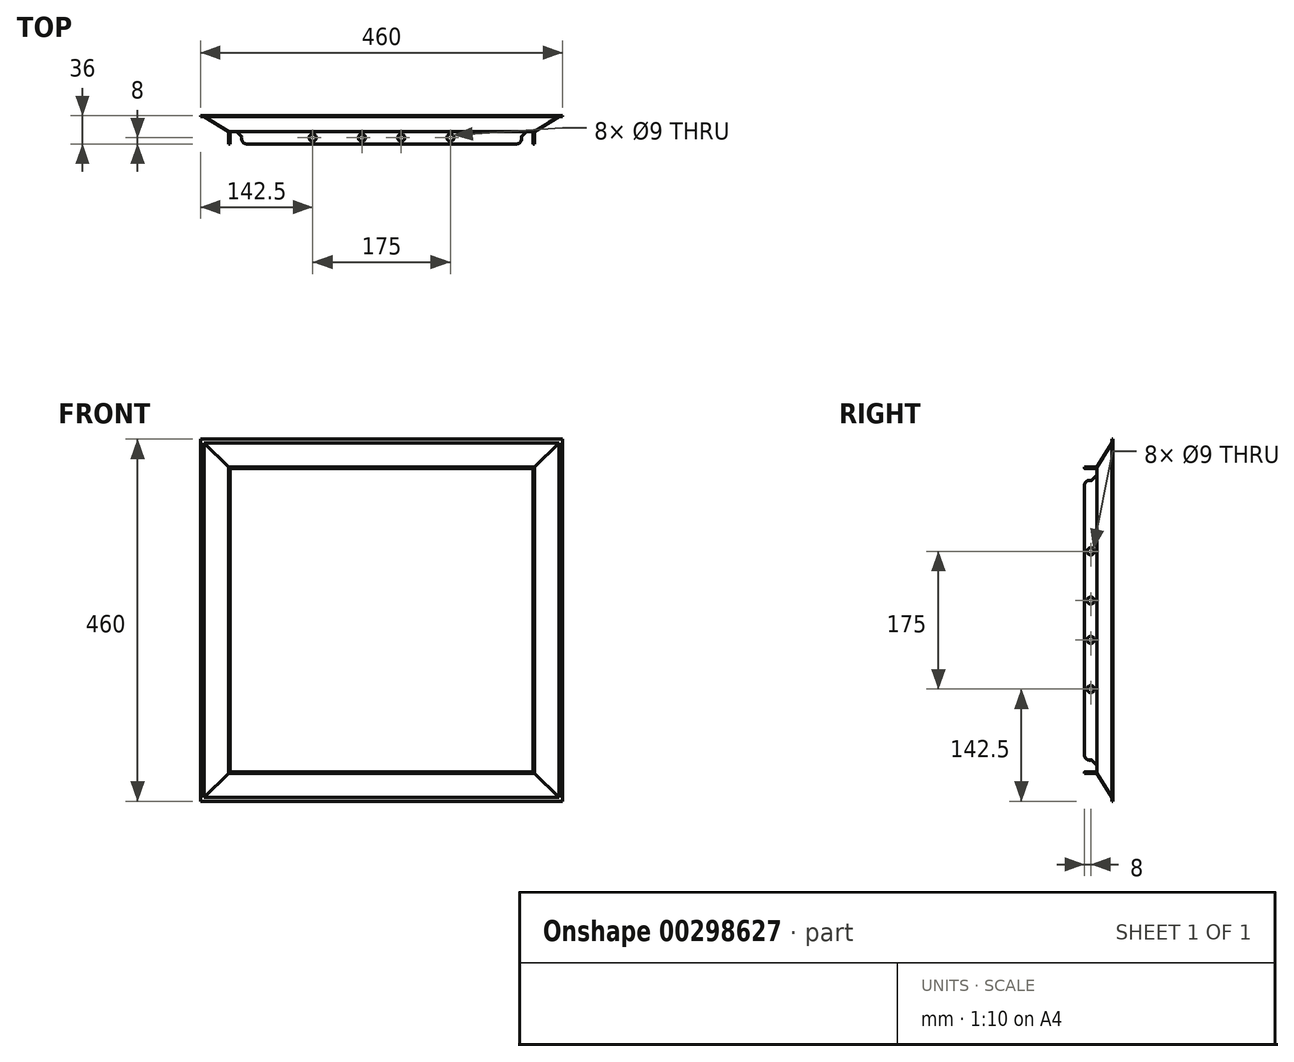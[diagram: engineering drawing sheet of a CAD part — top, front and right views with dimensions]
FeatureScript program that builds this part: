
annotation { "Feature Type Name" : "Feature", "Feature Type Description" : "" }
export const myFeature = defineFeature(function(context is Context, id is Id, definition is map)
    precondition{}
    {
        {
            var Q0;
            Q0=qCreatedBy(makeId("Front.planeOp"),FACE);
            var sketch = newSketch(context, id + "F0", { "sketchPlane" : qUnion([Q0])});
            skLineSegment(sketch, "E0.bottom", {"start": v(-230, 230) * mm, "end": v(230, 230) * mm});
            skLineSegment(sketch, "E0.top", {"start": v(-230, -230) * mm, "end": v(230, -230) * mm});
            skLineSegment(sketch, "E0.left", {"start": v(-230, 230) * mm, "end": v(-230, -230) * mm});
            skLineSegment(sketch, "E0.right", {"start": v(230, 230) * mm, "end": v(230, -230) * mm});
            skLineSegment(sketch, "E1.bottom", {"start": v(225, -225) * mm, "end": v(-225, -225) * mm});
            skLineSegment(sketch, "E1.top", {"start": v(225, 225) * mm, "end": v(-225, 225) * mm});
            skLineSegment(sketch, "E1.left", {"start": v(225, -225) * mm, "end": v(225, 225) * mm});
            skLineSegment(sketch, "E1.right", {"start": v(-225, -225) * mm, "end": v(-225, 225) * mm});
            skPoint(sketch, "E1.middle", {"position": v(0, 0) * mm});
            skLineSegment(sketch, "E2", {"start": v(442.73, 0) * mm, "end": v(-380.23, 0) * mm, "construction": true});
            skPoint(sketch, "E2.endSnap0", {"position": v(-225, 0) * mm});
            skLineSegment(sketch, "E3", {"start": v(0, -299.1) * mm, "end": v(0, 337.98) * mm, "construction": true});
            skSolve(sketch);
        }
        {
            var Q0;
            Q0=makeQuery(id+"F0.imprint","IMPRINT",FACE,{"disambiguationData":[TD([[makeQuery(id+"F0.imprint","IMPRINT",EDGE,{"derivedFrom":sQuery(id+"F0.wireOp",EDGE,"E0.bottom")}),-1.0]])]});
            cPlane(context, id + "F1", {"entities" : qUnion([Q0]), "cplaneType" : CPlaneType.OFFSET, "offset" : 20 * mm, "width" : 150 * mm, "height" : 150 * mm});
        }
        {
            var Q0;
            Q0=qCreatedBy(id+"F1.planeOp",FACE);
            var sketch = newSketch(context, id + "F2", { "sketchPlane" : qUnion([Q0])});
            skLineSegment(sketch, "E4.bottom", {"start": v(192.5, -192.5) * mm, "end": v(-192.5, -192.5) * mm});
            skLineSegment(sketch, "E4.top", {"start": v(192.5, 192.5) * mm, "end": v(-192.5, 192.5) * mm});
            skLineSegment(sketch, "E4.left", {"start": v(192.5, -192.5) * mm, "end": v(192.5, 192.5) * mm});
            skLineSegment(sketch, "E4.right", {"start": v(-192.5, -192.5) * mm, "end": v(-192.5, 192.5) * mm});
            skPoint(sketch, "E4.middle", {"position": v(0, 0) * mm});
            skSolve(sketch);
        }
        {
            var Q0;
            Q0=makeQuery(id+"F0.imprint","IMPRINT",FACE,{"disambiguationData":[TD([[makeQuery(id+"F0.imprint","IMPRINT",EDGE,{"derivedFrom":sQuery(id+"F0.wireOp",EDGE,"E1.bottom")}),-1.0]])]});
            var Q1;
            Q1=makeQuery(id+"F2.imprint","IMPRINT",FACE,{"disambiguationData":[TD([[makeQuery(id+"F2.imprint","IMPRINT",EDGE,{"derivedFrom":sQuery(id+"F2.wireOp",EDGE,"E4.bottom")}),-1.0]])]});
            loft(context, id + "F3", {"sheetProfilesArray" : [{ "sheetProfileEntities" : qUnion([Q0]) }, { "sheetProfileEntities" : qUnion([Q1]) }]});
        }
        {
            var Q0;
            Q0=makeQuery(id+"F3.opLoft","CAP_FACE",FACE,{"disambiguationData":[OSD([makeQuery(id+"F2.imprint","IMPRINT",FACE,{"disambiguationData":[TD([[makeQuery(id+"F2.imprint","IMPRINT",EDGE,{"derivedFrom":sQuery(id+"F2.wireOp",EDGE,"E4.bottom")}),-1.0]])]})])],"isStart":true});
            var Q1;
            Q1=makeQuery(id+"F3.opLoft","CAP_FACE",FACE,{"disambiguationData":[OSD([makeQuery(id+"F0.imprint","IMPRINT",FACE,{"disambiguationData":[TD([[makeQuery(id+"F0.imprint","IMPRINT",EDGE,{"derivedFrom":sQuery(id+"F0.wireOp",EDGE,"E1.bottom")}),-1.0]])]})])],"isStart":true});
            shell(context, id + "F4", {"entities" : qUnion([Q0, Q1]), "thickness" : 1 * mm, "oppositeDirection" : true});
        }
        {
            var Q0;
            Q0=makeQuery(id+"F0.imprint","IMPRINT",FACE,{"disambiguationData":[TD([[makeQuery(id+"F0.imprint","IMPRINT",EDGE,{"derivedFrom":sQuery(id+"F0.wireOp",EDGE,"E0.bottom")}),-1.0]])]});
            extrude(context, id + "F5", {"entities" : qUnion([Q0]), "operationType" : NewBodyOperationType.ADD, "depth" : 1 * mm});
        }
        {
            var Q0;
            Q0=makeQuery(id+"F3.opLoft","CAP_FACE",FACE,{"disambiguationData":[OSD([makeQuery(id+"F2.imprint","IMPRINT",FACE,{"disambiguationData":[TD([[makeQuery(id+"F2.imprint","IMPRINT",EDGE,{"derivedFrom":sQuery(id+"F2.wireOp",EDGE,"E4.bottom")}),-1.0]])]})])],"isStart":true});
            var sketch = newSketch(context, id + "F6", { "sketchPlane" : qUnion([Q0])});
            skLineSegment(sketch, "E5.0", {"start": v(-192.5, -192.5) * mm, "end": v(192.5, -192.5) * mm});
            skLineSegment(sketch, "E6.0", {"start": v(192.5, -192.5) * mm, "end": v(192.5, 192.5) * mm});
            skLineSegment(sketch, "E7.0", {"start": v(194.4, -194.4) * mm, "end": v(194.4, 194.4) * mm});
            skLineSegment(sketch, "E8.0", {"start": v(194.4, 194.4) * mm, "end": v(-194.4, 194.4) * mm});
            skLineSegment(sketch, "E9.0", {"start": v(192.5, 192.5) * mm, "end": v(-192.5, 192.5) * mm});
            skLineSegment(sketch, "E10.0", {"start": v(-194.4, 194.4) * mm, "end": v(-194.4, -194.4) * mm});
            skLineSegment(sketch, "E11.0", {"start": v(-192.5, 192.5) * mm, "end": v(-192.5, -192.5) * mm});
            skLineSegment(sketch, "E12.0", {"start": v(-194.4, -194.4) * mm, "end": v(194.4, -194.4) * mm});
            skSolve(sketch);
        }
        {
            var Q0;
            Q0 = qSketchRegion(id + "F6", true);
            extrude(context, id + "F7", {"entities" : qUnion([Q0]), "operationType" : NewBodyOperationType.ADD, "depth" : 16 * mm});
        }
        {
            var Q0;
            Q0=makeQuery(id+"F7.opExtrude","SWEPT_FACE",FACE,{"disambiguationData":[OSD([sQuery(id+"F6.wireOp",EDGE,"E8.0")])]});
            var sketch = newSketch(context, id + "F8", { "sketchPlane" : qUnion([Q0])});
            skLineSegment(sketch, "E13", {"start": v(194.4, -20) * mm, "end": v(184.4, -20) * mm});
            skLineSegment(sketch, "E14", {"start": v(184.4, -20) * mm, "end": v(177.34, -27.07) * mm});
            skArc(sketch, "E15", {"start": v(171.02, -36) * mm, "mid": v(176.49, -33.17) * mm, "end": v(177.34, -27.07) * mm});
            skLineSegment(sketch, "E16", {"start": v(194.4, -20) * mm, "end": v(194.4, -36) * mm});
            skLineSegment(sketch, "E17", {"start": v(171.02, -36) * mm, "end": v(194.4, -36) * mm});
            skLineSegment(sketch, "E18", {"start": v(-194.4, -20) * mm, "end": v(-184.4, -20) * mm});
            skLineSegment(sketch, "E19", {"start": v(-184.4, -20) * mm, "end": v(-177.34, -27.07) * mm});
            skArc(sketch, "E20", {"start": v(-177.34, -27.07) * mm, "mid": v(-176.49, -33.17) * mm, "end": v(-171.02, -36) * mm});
            skLineSegment(sketch, "E21", {"start": v(-171.02, -36) * mm, "end": v(-194.4, -36) * mm});
            skLineSegment(sketch, "E22", {"start": v(-194.4, -36) * mm, "end": v(-194.4, -20) * mm});
            skSolve(sketch);
        }
        {
            var Q0;
            Q0=makeQuery(id+"F8.imprint","IMPRINT",FACE,{"disambiguationData":[TD([[makeQuery(id+"F8.imprint","IMPRINT",EDGE,{"derivedFrom":sQuery(id+"F8.wireOp",EDGE,"E13")}),1.0]])]});
            var Q1;
            Q1=sQuery(id+"F8.wireOp",EDGE,"E16");
            revolve(context, id + "F9", {"operationType" : NewBodyOperationType.REMOVE, "entities" : qUnion([Q0]), "axis" : qUnion([Q1]), "revolveType" : RevolveType.FULL, "oppositeDirection" : true});
        }
        {
            var Q0;
            Q0=makeQuery(id+"F8.imprint","IMPRINT",FACE,{"disambiguationData":[TD([[makeQuery(id+"F8.imprint","IMPRINT",EDGE,{"derivedFrom":sQuery(id+"F8.wireOp",EDGE,"E18")}),1.0]])]});
            var Q1;
            Q1=sQuery(id+"F8.wireOp",EDGE,"E22");
            revolve(context, id + "F10", {"operationType" : NewBodyOperationType.REMOVE, "entities" : qUnion([Q0]), "axis" : qUnion([Q1]), "revolveType" : RevolveType.FULL, "oppositeDirection" : true});
        }
        {
            var Q0;
            Q0=makeQuery(id+"F7.opExtrude","SWEPT_FACE",FACE,{"disambiguationData":[OSD([sQuery(id+"F6.wireOp",EDGE,"E12.0")])]});
            var sketch = newSketch(context, id + "F11", { "sketchPlane" : qUnion([Q0])});
            skLineSegment(sketch, "E23.0", {"start": v(-171.02, 36) * mm, "end": v(-194.4, 36) * mm});
            skArc(sketch, "E24.0", {"start": v(-177.34, 27.07) * mm, "mid": v(-176.49, 33.17) * mm, "end": v(-171.02, 36) * mm});
            skLineSegment(sketch, "E24.1", {"start": v(-194.4, 36) * mm, "end": v(-194.4, 20) * mm});
            skLineSegment(sketch, "E24.2", {"start": v(-184.4, 20) * mm, "end": v(-177.34, 27.07) * mm});
            skLineSegment(sketch, "E25.0", {"start": v(-194.4, 20) * mm, "end": v(-184.4, 20) * mm});
            skLineSegment(sketch, "E26.0", {"start": v(171.02, 36) * mm, "end": v(194.4, 36) * mm});
            skLineSegment(sketch, "E27.0", {"start": v(194.4, 20) * mm, "end": v(194.4, 36) * mm});
            skArc(sketch, "E28.0", {"start": v(171.02, 36) * mm, "mid": v(176.49, 33.17) * mm, "end": v(177.34, 27.07) * mm});
            skLineSegment(sketch, "E29.0", {"start": v(184.4, 20) * mm, "end": v(177.34, 27.07) * mm});
            skLineSegment(sketch, "E30.0", {"start": v(194.4, 20) * mm, "end": v(184.4, 20) * mm});
            skSolve(sketch);
        }
        {
            var Q0;
            Q0=makeQuery(id+"F11.imprint","IMPRINT",FACE,{"disambiguationData":[TD([[makeQuery(id+"F11.imprint","IMPRINT",EDGE,{"derivedFrom":sQuery(id+"F11.wireOp",EDGE,"E26.0")}),-1.0]])]});
            var Q1;
            Q1=sQuery(id+"F11.wireOp",EDGE,"E27.0");
            revolve(context, id + "F12", {"operationType" : NewBodyOperationType.REMOVE, "entities" : qUnion([Q0]), "axis" : qUnion([Q1]), "revolveType" : RevolveType.FULL, "oppositeDirection" : true});
        }
        {
            var Q0;
            Q0=makeQuery(id+"F11.imprint","IMPRINT",FACE,{"disambiguationData":[TD([[makeQuery(id+"F11.imprint","IMPRINT",EDGE,{"derivedFrom":sQuery(id+"F11.wireOp",EDGE,"E23.0")}),-1.0]])]});
            var Q1;
            Q1=sQuery(id+"F11.wireOp",EDGE,"E24.1");
            revolve(context, id + "F13", {"operationType" : NewBodyOperationType.REMOVE, "entities" : qUnion([Q0]), "axis" : qUnion([Q1]), "revolveType" : RevolveType.FULL, "oppositeDirection" : true});
        }
        {
            var Q0;
            Q0=makeQuery(id+"F7.opExtrude","SWEPT_FACE",FACE,{"disambiguationData":[OSD([sQuery(id+"F6.wireOp",EDGE,"E12.0")])]});
            var sketch = newSketch(context, id + "F14", { "sketchPlane" : qUnion([Q0])});
            skLineSegment(sketch, "E31", {"start": v(-272.07, 28) * mm, "end": v(274.69, 28) * mm, "construction": true});
            skCircle(sketch, "E32", {"center": v(-87.5, 28) * mm, "radius": 4.5 * mm});
            skCircle(sketch, "E33", {"center": v(-25, 28) * mm, "radius": 4.5 * mm});
            skCircle(sketch, "E34", {"center": v(25, 28) * mm, "radius": 4.5 * mm});
            skCircle(sketch, "E35", {"center": v(87.5, 28) * mm, "radius": 4.5 * mm});
            skSolve(sketch);
        }
        {
            var Q0;
            Q0=makeQuery(id+"F14.imprint","IMPRINT",FACE,{"disambiguationData":[TD([[makeQuery(id+"F14.imprint","IMPRINT",EDGE,{"derivedFrom":sQuery(id+"F14.wireOp",EDGE,"E32")}),1.0]])]});
            var Q1;
            Q1=makeQuery(id+"F14.imprint","IMPRINT",FACE,{"disambiguationData":[TD([[makeQuery(id+"F14.imprint","IMPRINT",EDGE,{"derivedFrom":sQuery(id+"F14.wireOp",EDGE,"E33")}),1.0]])]});
            var Q2;
            Q2=makeQuery(id+"F14.imprint","IMPRINT",FACE,{"disambiguationData":[TD([[makeQuery(id+"F14.imprint","IMPRINT",EDGE,{"derivedFrom":sQuery(id+"F14.wireOp",EDGE,"E34")}),1.0]])]});
            var Q3;
            Q3=makeQuery(id+"F14.imprint","IMPRINT",FACE,{"disambiguationData":[TD([[makeQuery(id+"F14.imprint","IMPRINT",EDGE,{"derivedFrom":sQuery(id+"F14.wireOp",EDGE,"E35")}),1.0]])]});
            extrude(context, id + "F15", {"entities" : qUnion([Q0, Q1, Q2, Q3]), "operationType" : NewBodyOperationType.REMOVE, "endBound" : BoundingType.THROUGH_ALL, "oppositeDirection" : true, "depth" : 25 * mm});
        }
        {
            var Q0;
            Q0=makeQuery(id+"F7.opExtrude","SWEPT_FACE",FACE,{"disambiguationData":[OSD([sQuery(id+"F6.wireOp",EDGE,"E7.0")])]});
            var sketch = newSketch(context, id + "F16", { "sketchPlane" : qUnion([Q0])});
            skLineSegment(sketch, "E36", {"start": v(-28, -153.4) * mm, "end": v(-28, 164.11) * mm, "construction": true});
            skCircle(sketch, "E37", {"center": v(-28, -87.5) * mm, "radius": 4.5 * mm});
            skCircle(sketch, "E38", {"center": v(-28, -25) * mm, "radius": 4.5 * mm});
            skCircle(sketch, "E39", {"center": v(-28, 25) * mm, "radius": 4.5 * mm});
            skCircle(sketch, "E40", {"center": v(-28, 87.5) * mm, "radius": 4.5 * mm});
            skSolve(sketch);
        }
        {
            var Q0;
            Q0=makeQuery(id+"F16.imprint","IMPRINT",FACE,{"disambiguationData":[TD([[makeQuery(id+"F16.imprint","IMPRINT",EDGE,{"derivedFrom":sQuery(id+"F16.wireOp",EDGE,"E37")}),1.0]])]});
            var Q1;
            Q1=makeQuery(id+"F16.imprint","IMPRINT",FACE,{"disambiguationData":[TD([[makeQuery(id+"F16.imprint","IMPRINT",EDGE,{"derivedFrom":sQuery(id+"F16.wireOp",EDGE,"E38")}),1.0]])]});
            var Q2;
            Q2=makeQuery(id+"F16.imprint","IMPRINT",FACE,{"disambiguationData":[TD([[makeQuery(id+"F16.imprint","IMPRINT",EDGE,{"derivedFrom":sQuery(id+"F16.wireOp",EDGE,"E39")}),1.0]])]});
            var Q3;
            Q3=makeQuery(id+"F16.imprint","IMPRINT",FACE,{"disambiguationData":[TD([[makeQuery(id+"F16.imprint","IMPRINT",EDGE,{"derivedFrom":sQuery(id+"F16.wireOp",EDGE,"E40")}),1.0]])]});
            extrude(context, id + "F17", {"entities" : qUnion([Q0, Q1, Q2, Q3]), "operationType" : NewBodyOperationType.REMOVE, "endBound" : BoundingType.THROUGH_ALL, "oppositeDirection" : true, "depth" : 25 * mm});
        }
    });
